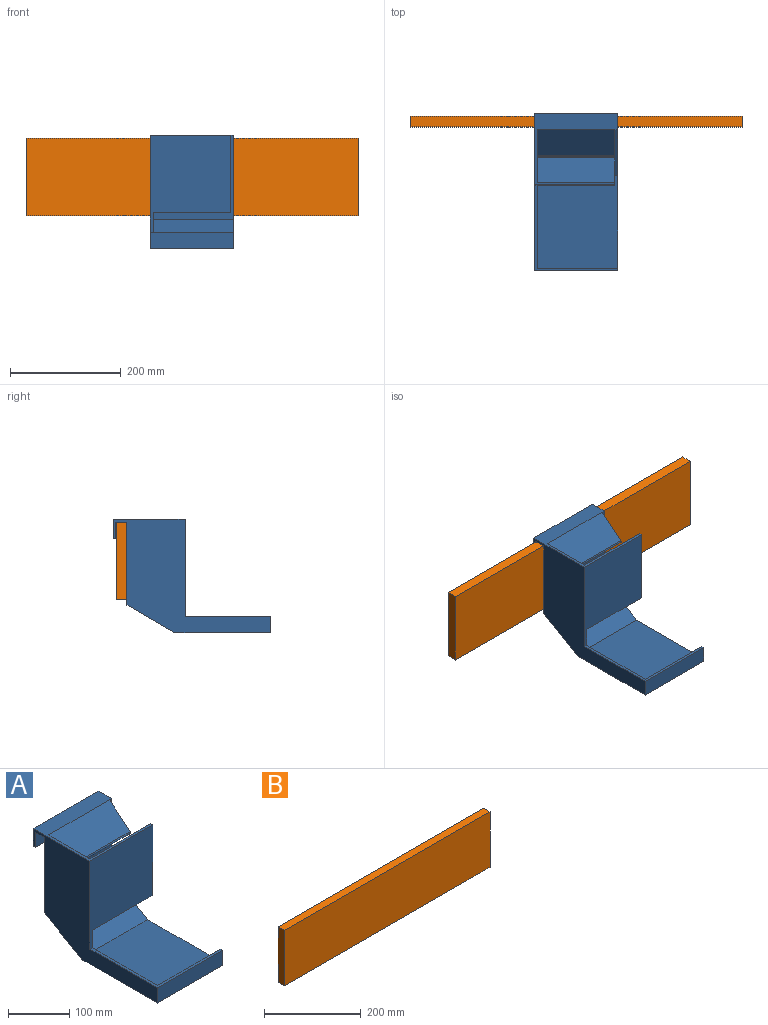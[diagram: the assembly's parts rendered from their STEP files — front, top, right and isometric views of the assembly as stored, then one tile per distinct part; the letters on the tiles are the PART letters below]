
ASSEMBLY  parts=2 mates=2
PART A: 29 faces, bbox 150x285x205 mm
  f0: plane 250x200mm, normal (1,0,0), area 20469.4mm2, adj f1,f7,f8,f9,f10,f11,f12,f18
  f1: plane 140x93.33mm, normal (0,1,0), area 13066.7mm2, adj f0,f7,f19,f26
  f2: plane 150x150mm, normal (0,1,0), area 22500mm2, adj f3,f15,f16,f17
  f3: plane 150x20mm, normal (0,0,-1), area 3000mm2, adj f2,f4,f16,f17
  f4: plane 150x30mm, normal (0,-1,0), area 4500mm2, adj f3,f5,f16,f17
  f5: plane 150x5mm, normal (0,0,-1), area 750mm2, adj f4,f6,f16,f17
  f6: plane 150x35mm, normal (0,1,0), area 5250mm2, adj f5,f7,f16,f17
  f7: plane 150x130mm, normal (0,0,1), area 5700mm2, adj f0,f1,f6,f8,f16,f17,f18,f19
  f8: plane 152.11x145mm, normal (0,-1,0), area 21142.6mm2, adj f0,f7,f9,f16,f24,f25
  f9: plane 145x82.94mm, normal (0,-0.5,0.87), area 13887.2mm2, adj f0,f8,f10,f16
  f10: plane 167.06x145mm, normal (0,0,1), area 24223.4mm2, adj f0,f9,f11,f16
  f11: plane 145x25mm, normal (0,1,0), area 3625mm2, adj f0,f10,f12,f16
  f12: plane 155x150mm, normal (0,0,1), area 1500mm2, adj f0,f11,f13,f16,f17,f18
  f13: plane 150x30mm, normal (0,-1,0), area 4500mm2, adj f12,f14,f16,f17
  f14: plane 173.4x150mm, normal (0,0,-1), area 26009.6mm2, adj f13,f15,f16,f17
  f15: plane 150x86.6mm, normal (0,0.5,-0.87), area 15000mm2, adj f2,f14,f16,f17
  f16: plane 285x205mm, normal (1,0,0), area 2520.9mm2, adj f2,f3,f4,f5,f6,f7,f8,f9
  f17: plane 285x205mm, normal (-1,0,0), area 24284.9mm2, adj f2,f3,f4,f5,f6,f7,f12,f13
  f18: plane 175x145mm, normal (0,-1,0), area 20475mm2, adj f0,f7,f12,f17,f19,f21
  f19: plane 140x49.94mm, normal (1,0,0), area 986.8mm2, adj f1,f7,f18,f20,f21,f26,f27,f28
  f20: plane 140x40.14mm, normal (0,1,0), area 5619.5mm2, adj f0,f19,f21,f27
  f21: plane 140x5mm, normal (0,0,-1), area 700mm2, adj f0,f18,f19,f20
  f22: plane 140x47.26mm, normal (0,-0.64,0.77), area 8637.4mm2, adj f0,f7,f23,f25
  f23: cylinder r=2.5mm len=140mm, axis (-1,0,0), area 1099.6mm2, adj f0,f22,f24,f25
  f24: plane 140x44.05mm, normal (0,0.64,-0.77), area 8050mm2, adj f0,f8,f23,f25
  f25: plane 48.15x44.07mm, normal (1,0,0), area 307.8mm2, adj f8,f22,f23,f24
  f26: plane 140x44.05mm, normal (0,0.64,0.77), area 8050mm2, adj f0,f1,f19,f28
  f27: plane 140x40.83mm, normal (0,-0.64,-0.77), area 7462.6mm2, adj f0,f19,f20,f28
  f28: cylinder r=2.5mm len=140mm, axis (-1,0,0), area 1099.6mm2, adj f0,f19,f26,f27
PART B: 6 faces, bbox 600x19x140 mm
  f0: plane 600x19mm, normal (0,0,1), area 11400mm2, adj f1,f3,f4,f5
  f1: plane 600x140mm, normal (0,-1,0), area 84000mm2, adj f0,f2,f4,f5
  f2: plane 600x19mm, normal (0,0,-1), area 11400mm2, adj f1,f3,f4,f5
  f3: plane 600x140mm, normal (0,1,0), area 84000mm2, adj f0,f2,f4,f5
  f4: plane 140x19mm, normal (1,0,0), area 2660mm2, adj f0,f1,f2,f3
  f5: plane 140x19mm, normal (-1,0,0), area 2660mm2, adj f0,f1,f2,f3
PLACE A t=(189.44,105.93,14.13)mm
PLACE B t=(-35.56,105.93,14.13)mm fixed
MATE planar A.f2 <-> B.f1  axis (0,1,0) through (264.44,105.93,-60.87)mm
MATE planar A.f3 <-> B.f0  axis (0,0,-1) through (264.44,115.93,14.13)mm
